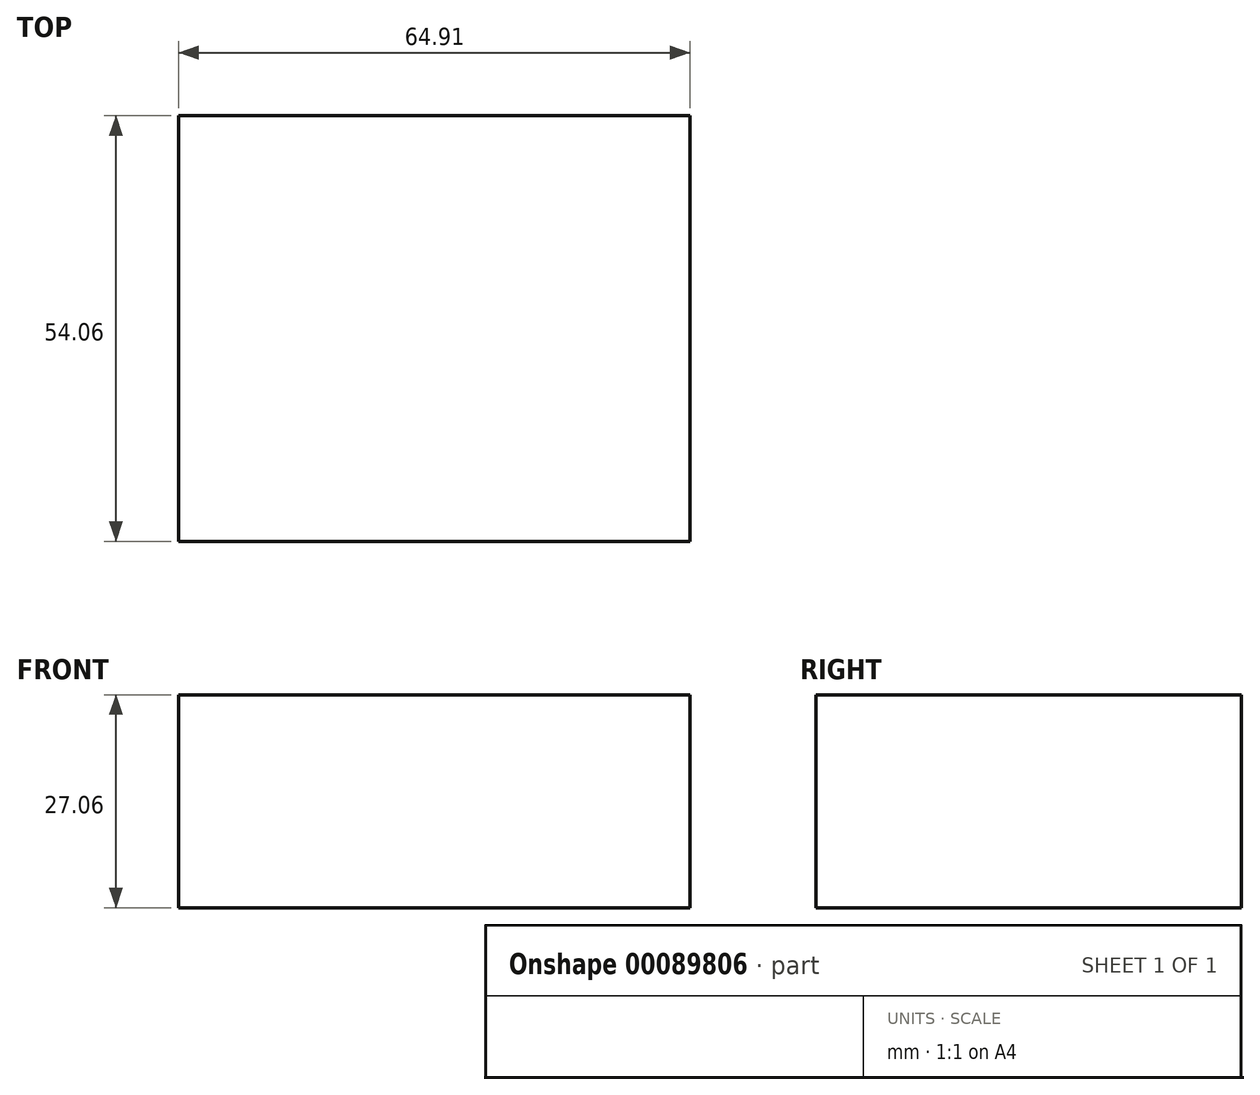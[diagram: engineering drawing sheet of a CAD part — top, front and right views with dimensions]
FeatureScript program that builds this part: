
annotation { "Feature Type Name" : "Feature", "Feature Type Description" : "" }
export const myFeature = defineFeature(function(context is Context, id is Id, definition is map)
    precondition{}
    {
        {
            var Q0;
            Q0=qCreatedBy(makeId("Top.planeOp"),FACE);
            var sketch = newSketch(context, id + "F0", { "sketchPlane" : qUnion([Q0])});
            skLineSegment(sketch, "E0.bottom", {"start": v(0, 0) * mm, "end": v(64.91, 0) * mm});
            skLineSegment(sketch, "E0.top", {"start": v(0, -54.06) * mm, "end": v(64.91, -54.06) * mm});
            skLineSegment(sketch, "E0.left", {"start": v(0, 0) * mm, "end": v(0, -54.06) * mm});
            skLineSegment(sketch, "E0.right", {"start": v(64.91, 0) * mm, "end": v(64.91, -54.06) * mm});
            skSolve(sketch);
        }
        {
            var Q0;
            Q0=makeQuery(id+"F0.imprint","IMPRINT",FACE,{"disambiguationData":[TD([[makeQuery(id+"F0.imprint","IMPRINT",EDGE,{"derivedFrom":sQuery(id+"F0.wireOp",EDGE,"E0.bottom")}),-1.0]])]});
            extrude(context, id + "F1", {"entities" : qUnion([Q0]), "depth" : 27.06 * mm});
        }
    });
